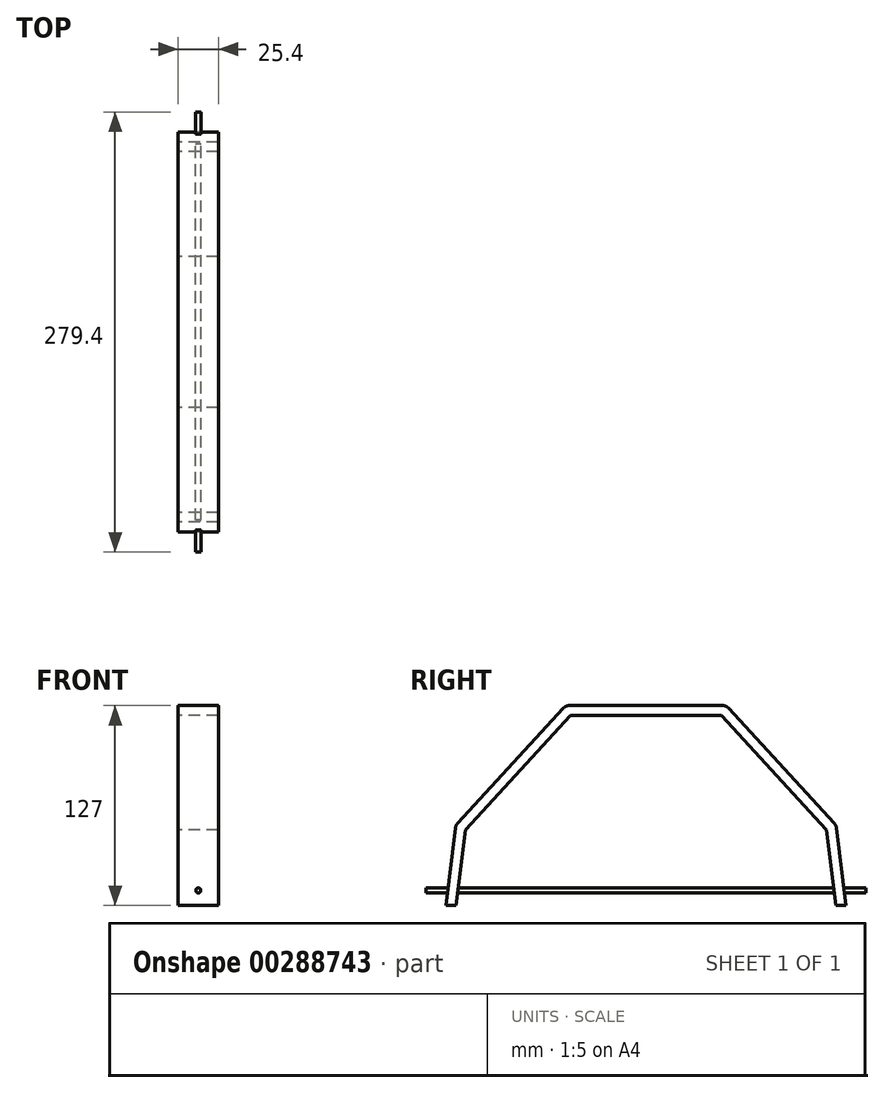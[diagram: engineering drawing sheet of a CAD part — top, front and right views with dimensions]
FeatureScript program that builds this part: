
annotation { "Feature Type Name" : "Feature", "Feature Type Description" : "" }
export const myFeature = defineFeature(function(context is Context, id is Id, definition is map)
    precondition{}
    {
        {
            var Q0;
            Q0=qCreatedBy(makeId("Right.planeOp"),FACE);
            var sketch = newSketch(context, id + "F0", { "sketchPlane" : qUnion([Q0])});
            skLineSegment(sketch, "E0", {"start": v(0, 68.5) * mm, "end": v(0, -29.99) * mm, "construction": true});
            skLineSegment(sketch, "E1", {"start": v(-127, 0) * mm, "end": v(-120.8, 50.8) * mm});
            skLineSegment(sketch, "E2", {"start": v(-120.8, 50.8) * mm, "end": v(-50.8, 127) * mm});
            skLineSegment(sketch, "E3", {"start": v(-50.8, 127) * mm, "end": v(0, 127) * mm});
            skLineSegment(sketch, "E4.MirrorCS", {"start": v(120.8, 50.8) * mm, "end": v(50.8, 127) * mm});
            skLineSegment(sketch, "E5.MirrorCS", {"start": v(50.8, 127) * mm, "end": v(0, 127) * mm});
            skLineSegment(sketch, "E6.MirrorCS", {"start": v(127, 0) * mm, "end": v(120.8, 50.8) * mm});
            skLineSegment(sketch, "E7.0", {"start": v(-120.6, 0) * mm, "end": v(-114.75, 48) * mm});
            skLineSegment(sketch, "E7.1", {"start": v(-114.75, 48) * mm, "end": v(-48.01, 120.65) * mm});
            skLineSegment(sketch, "E7.2", {"start": v(120.6, 0) * mm, "end": v(114.75, 48) * mm});
            skLineSegment(sketch, "E7.3", {"start": v(114.75, 48) * mm, "end": v(48.01, 120.65) * mm});
            skLineSegment(sketch, "E7.4", {"start": v(48.01, 120.65) * mm, "end": v(0, 120.65) * mm});
            skLineSegment(sketch, "E7.5", {"start": v(-48.01, 120.65) * mm, "end": v(0, 120.65) * mm});
            skLineSegment(sketch, "E8", {"start": v(-127, 0) * mm, "end": v(-120.6, 0) * mm});
            skLineSegment(sketch, "E9", {"start": v(127, 0) * mm, "end": v(120.6, 0) * mm});
            skSolve(sketch);
        }
        {
            var Q0;
            Q0 = qSketchRegion(id + "F0", true);
            extrude(context, id + "F1", {"entities" : qUnion([Q0]), "endBound" : BoundingType.SYMMETRIC, "depth" : 25.4 * mm});
        }
        {
            var Q0;
            Q0=makeQuery(id+"F1.opExtrude","SWEPT_EDGE",EDGE,{"disambiguationData":[OSD([sQuery(id+"F0.wireOp",EDGE,"E1"),sQuery(id+"F0.wireOp",EDGE,"E2")])]});
            var Q1;
            Q1=makeQuery(id+"F1.opExtrude","SWEPT_EDGE",EDGE,{"disambiguationData":[OSD([sQuery(id+"F0.wireOp",EDGE,"E4.MirrorCS"),sQuery(id+"F0.wireOp",EDGE,"E6.MirrorCS")])]});
            var Q2;
            Q2=makeQuery(id+"F1.opExtrude","SWEPT_EDGE",EDGE,{"disambiguationData":[OSD([sQuery(id+"F0.wireOp",EDGE,"E2"),sQuery(id+"F0.wireOp",EDGE,"E3")])]});
            var Q3;
            Q3=makeQuery(id+"F1.opExtrude","SWEPT_EDGE",EDGE,{"disambiguationData":[OSD([sQuery(id+"F0.wireOp",EDGE,"E4.MirrorCS"),sQuery(id+"F0.wireOp",EDGE,"E5.MirrorCS")])]});
            fillet(context, id + "F2", {"entities" : qUnion([Q0, Q1, Q2, Q3]), "radius" : 5.08 * mm, "tangentPropagation" : true, "allowEdgeOverflow" : false});
        }
        {
            var Q0;
            Q0=qCreatedBy(makeId("Front.planeOp"),FACE);
            var sketch = newSketch(context, id + "F3", { "sketchPlane" : qUnion([Q0])});
            skCircle(sketch, "E10", {"center": v(0, 9.53) * mm, "radius": 1.59 * mm});
            skSolve(sketch);
        }
        {
            var Q0;
            Q0 = qSketchRegion(id + "F3", true);
            extrude(context, id + "F4", {"entities" : qUnion([Q0]), "operationType" : NewBodyOperationType.REMOVE, "endBound" : BoundingType.SYMMETRIC, "oppositeDirection" : true, "depth" : 508 * mm});
        }
        {
            var Q0;
            Q0=qCreatedBy(makeId("Front.planeOp"),FACE);
            var sketch = newSketch(context, id + "F5", { "sketchPlane" : qUnion([Q0])});
            skCircle(sketch, "E11", {"center": v(0, 9.53) * mm, "radius": 1.59 * mm});
            skSolve(sketch);
        }
        {
            var Q0;
            Q0 = qSketchRegion(id + "F5", true);
            extrude(context, id + "F6", {"entities" : qUnion([Q0]), "operationType" : NewBodyOperationType.ADD, "endBound" : BoundingType.SYMMETRIC, "depth" : 279.4 * mm});
        }
    });
